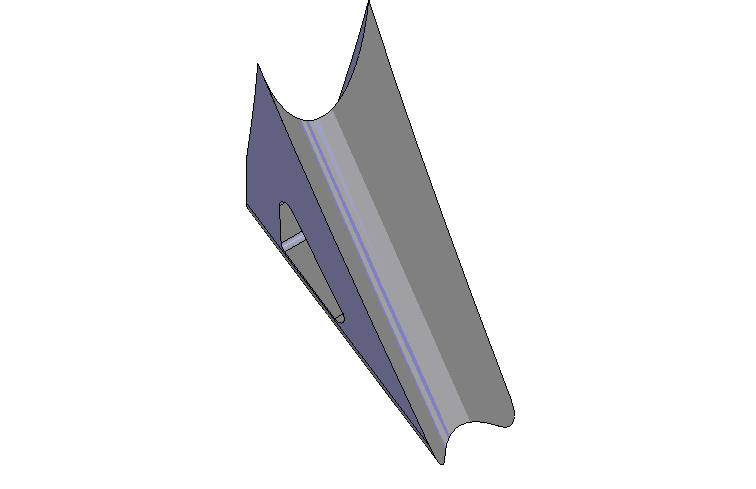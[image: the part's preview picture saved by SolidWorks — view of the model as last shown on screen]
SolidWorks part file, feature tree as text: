
SOLIDWORKS PART (.sldprt)
format: sldprt  version: not decoded by parser v0  size: 403,968 bytes
history: native  units: mm
features: plane x11, sketch x10, material x1, extrude x1, cut_extrude x1, cut_revolve x1 (+10 scaffold rows collapsed)
feature tree (35):
  scaffold x10  (default folders/planes/origin — collapsed)
  material  "Matériau <non spécifié>"
  plane  "Plan de face"
  plane  "Plan de dessus"
  plane  "Plan de droite"
  sketch  "Esquisse1"  dims[c1.D1=625.0mm c1.D2=460.0mm c1.D3=545.0mm c1.D4=27.0mm c1.D5=500.0mm c1.D6=445.0mm c1.D7=670.0mm c2.D1=622.0mm c2.D2=670.0mm c2.D3=545.0mm c2.D4=460.0mm c2.D5=445.0mm c2.D6=495.0mm c2.D7=535.0mm c2.D8=27.0mm c2.D9=8.0mm c2.D10=155.0mm c2.D11=400.0mm c2.D12=~545.374305mm c3.D12=56.0deg]
  plane  "Plan1"
  plane  "Plan2"  Offset=180mm
  plane  "Plan3"  Offset=340mm
  plane  "Plan4"  Offset=500mm
  plane  "Plan5"
  plane  "Plan7"
  plane  "Plan8"
  sketch  "Esquisse5"  dims[c1.D1=42.0mm c1.D2=55.0mm c1.D3=2.0mm c1.D4=~8.95384mm c2.D3=2.0mm c2.D4=2.0mm]
  sketch  "Esquisse6"  dims[D1=50.0mm D2=46.0mm]
  sketch  "Esquisse7"  dims[D1=46.0mm]
  sketch  "Esquisse8"
  sketch  "Esquisse9"  dims[D1=45.0mm D2=41.0mm]
  sketch  "Esquisse10"  dims[c1.D1=~387.763491mm c2.D1=20.0deg c2.D2=72.0mm c3.D1=192.0mm]
  plane  "Plan6"
  sketch  "Esquisse11"  dims[c1.D1=5.0mm c1.D5=41.0mm c1.D2=40.0mm c1.D3=28.0mm c1.D4=~61.817983mm c2.D4=17.0deg c2.D2=60.0mm]
  extrude  "Extrusion1"  [1 undecoded]
  sketch  "Esquisse12"  dims[D6=2.5mm D1=5.0mm D2=21.0mm D3=50.0mm D4=36.0mm D5=34.0mm]
  cut_extrude  "Enlèv. mat.-Extru.1"  [1 undecoded]
  sketch  "Esquisse3"  dims[c1.D1=50.0mm c1.D2=45.0mm c1.D3=~233.713088mm c2.D2=140.0mm c2.D3=45.0mm c2.D4=9.0mm c2.D5=80.0mm c2.D6=27.0mm]
  cut_revolve  "Enlèvement de matière-Révolution1"  Angle=360deg
decode coverage: 10 of 13 modeling features carry decoded parameters
note: ~ marks probable driven/reference dimensions
note: 2 parameter values undecoded
note: suppression state not decoded; provenance and decode notes live in map.json
